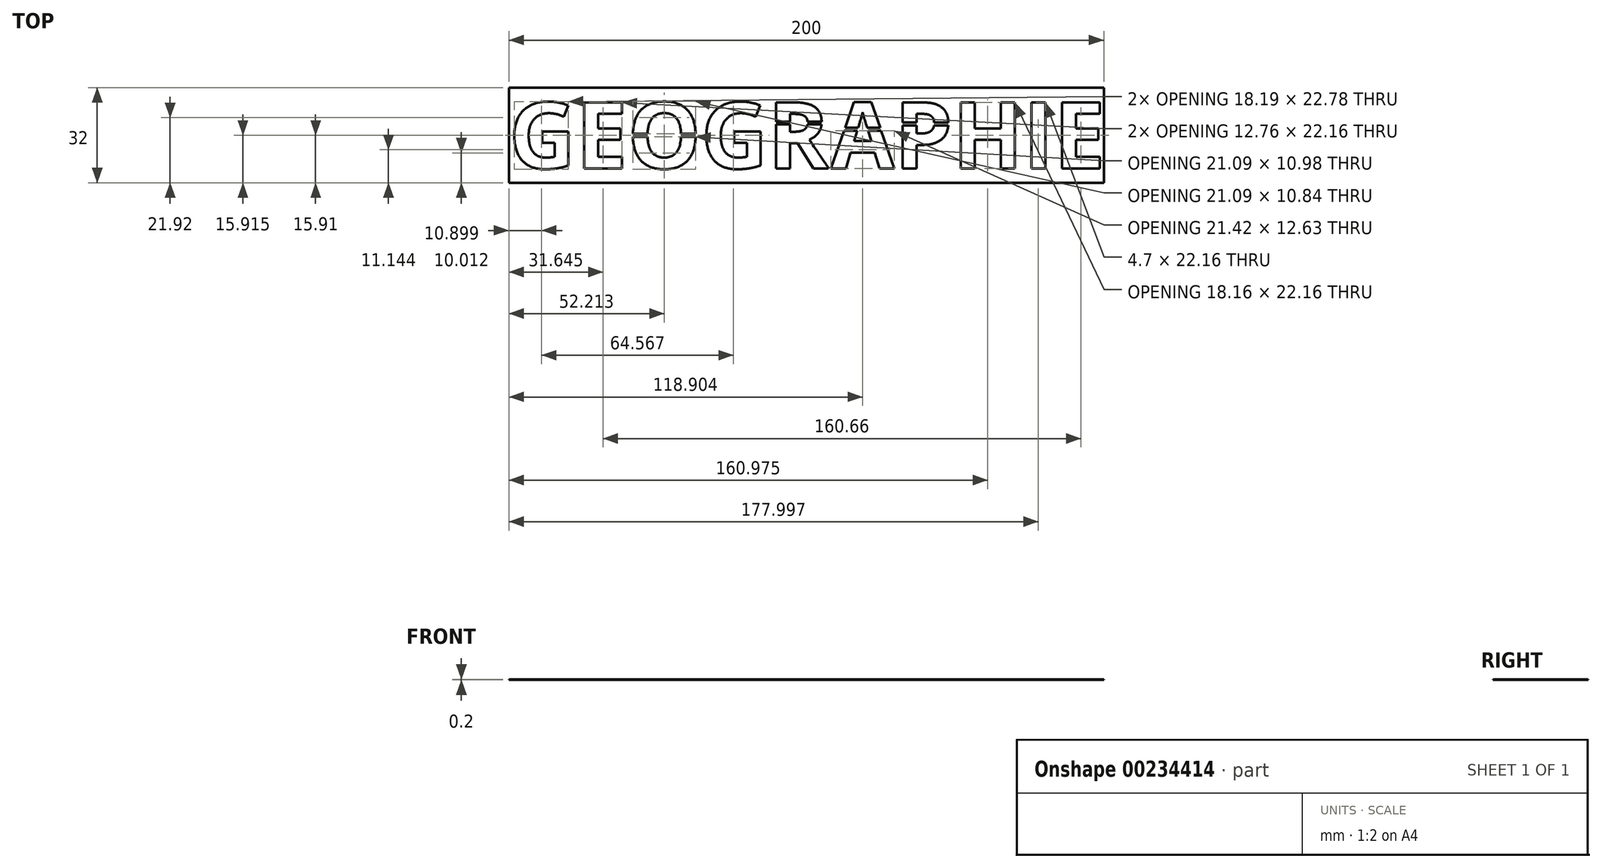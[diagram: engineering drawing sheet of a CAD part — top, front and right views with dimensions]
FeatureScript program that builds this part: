
annotation { "Feature Type Name" : "Feature", "Feature Type Description" : "" }
export const myFeature = defineFeature(function(context is Context, id is Id, definition is map)
    precondition{}
    {
        {
            var Q0;
            Q0=qCreatedBy(makeId("Top.planeOp"),FACE);
            var sketch = newSketch(context, id + "F0", { "sketchPlane" : qUnion([Q0])});
            skLineSegment(sketch, "E0.bottom", {"start": v(0, 0) * mm, "end": v(200, 0) * mm});
            skLineSegment(sketch, "E0.top", {"start": v(0, 32) * mm, "end": v(200, 32) * mm});
            skLineSegment(sketch, "E0.left", {"start": v(0, 0) * mm, "end": v(0, 32) * mm});
            skLineSegment(sketch, "E0.right", {"start": v(200, 0) * mm, "end": v(200, 32) * mm});
            skPoint(sketch, "E1", {"position": v(0, 16) * mm});
            skPoint(sketch, "E2", {"position": v(22.5, 32) * mm});
            skPoint(sketch, "E3", {"position": v(40, 32) * mm});
            skPoint(sketch, "E4", {"position": v(64.5, 32) * mm});
            skPoint(sketch, "E5", {"position": v(87, 32) * mm});
            skPoint(sketch, "E6", {"position": v(107.5, 32) * mm});
            skPoint(sketch, "E7", {"position": v(130, 32) * mm});
            skPoint(sketch, "E8", {"position": v(149, 32) * mm});
            skPoint(sketch, "E9", {"position": v(172, 32) * mm});
            skPoint(sketch, "E10", {"position": v(182.5, 32) * mm});
            skLineSegment(sketch, "E11", {"start": v(22.5, 32) * mm, "end": v(22.5, 0) * mm, "construction": true});
            skLineSegment(sketch, "E12", {"start": v(40, 32) * mm, "end": v(40, 0) * mm, "construction": true});
            skLineSegment(sketch, "E13", {"start": v(64.5, 32) * mm, "end": v(64.5, 0) * mm, "construction": true});
            skPoint(sketch, "E14", {"position": v(22.5, 16) * mm});
            skPoint(sketch, "E15", {"position": v(40, 16) * mm});
            skPoint(sketch, "E16", {"position": v(64.5, 16) * mm});
            skLineSegment(sketch, "E17", {"start": v(40, 16.5) * mm, "end": v(64.5, 16.5) * mm});
            skLineSegment(sketch, "E18", {"start": v(40, 16) * mm, "end": v(64.5, 16) * mm, "construction": true});
            skLineSegment(sketch, "E19.MirrorCS", {"start": v(40, 15.5) * mm, "end": v(64.5, 15.5) * mm});
            skLineSegment(sketch, "E20", {"start": v(87, 32) * mm, "end": v(87, 0) * mm, "construction": true});
            skLineSegment(sketch, "E21", {"start": v(130, 32) * mm, "end": v(130, 0) * mm, "construction": true});
            skLineSegment(sketch, "E22", {"start": v(149, 32) * mm, "end": v(149, 0) * mm, "construction": true});
            skLineSegment(sketch, "E23", {"start": v(172, 32) * mm, "end": v(172, 0) * mm, "construction": true});
            skLineSegment(sketch, "E24", {"start": v(182.5, 32) * mm, "end": v(182.5, 0) * mm, "construction": true});
            skLineSegment(sketch, "E25", {"start": v(107.7, 17.96) * mm, "end": v(130, 17.96) * mm, "construction": true});
            skLineSegment(sketch, "E26", {"start": v(107.7, 18.46) * mm, "end": v(130, 18.46) * mm});
            skLineSegment(sketch, "E27.MirrorCS", {"start": v(107.7, 17.46) * mm, "end": v(130, 17.46) * mm});
            skLineSegment(sketch, "E28", {"start": v(130, 19.8) * mm, "end": v(149, 19.8) * mm, "construction": true});
            skLineSegment(sketch, "E29", {"start": v(130, 20.3) * mm, "end": v(149, 20.3) * mm});
            skLineSegment(sketch, "E30.MirrorCS", {"start": v(130, 19.3) * mm, "end": v(149, 19.3) * mm});
            skText(sketch, "E31", { "text": "GEOGRAPHIE", "fontName": "OpenSans-Bold.ttf"});
            skLineSegment(sketch, "E32", {"start": v(107.33, 32) * mm, "end": v(107.33, 0) * mm});
            skLineSegment(sketch, "E33", {"start": v(107.7, 0) * mm, "end": v(107.7, 32) * mm});
            skLineSegment(sketch, "E34", {"start": v(87, 20.08) * mm, "end": v(107.33, 20.08) * mm, "construction": true});
            skLineSegment(sketch, "E35", {"start": v(87, 20.58) * mm, "end": v(107.33, 20.58) * mm});
            skLineSegment(sketch, "E36.MirrorCS", {"start": v(87, 19.58) * mm, "end": v(107.33, 19.58) * mm});
            const initialGuessF0  = {"E31": [0, 0.00483, 1, 0, 0.02235]};
            skSetInitialGuess(sketch, initialGuessF0);
            skSolve(sketch);
        }
        {
            var Q0;
            {var subQ5=sQuery(id+"F0.wireOp",EDGE,"E31.sketch_text.stroke-40");Q0=makeQuery(id+"F0.imprint","IMPRINT",FACE,{"disambiguationData":[TD([[makeQuery(id+"F0.imprint","IMPRINT",EDGE,{"derivedFrom":subQ5}),1.0]])]});}
            var Q1;
            {var subQ5=sQuery(id+"F0.wireOp",EDGE,"E31.sketch_text.stroke-44");var subQ9=sQuery(id+"F0.wireOp",EDGE,"E17");var subQ10=makeQuery(id+"F0.imprint","INTERSECT",VERTEX,{"derivedFrom":[subQ9,subQ5]});Q1=makeQuery(id+"F0.imprint","IMPRINT",FACE,{"disambiguationData":[TD([[makeQuery(id+"F0.imprint","IMPRINT",EDGE,{"disambiguationData":[TD([[subQ10,-1.0]])],"derivedFrom":subQ9}),-1.0]])]});}
            var Q2;
            {var subQ5=sQuery(id+"F0.wireOp",EDGE,"E31.sketch_text.stroke-43");Q2=makeQuery(id+"F0.imprint","IMPRINT",FACE,{"disambiguationData":[TD([[makeQuery(id+"F0.imprint","IMPRINT",EDGE,{"derivedFrom":subQ5}),1.0]])]});}
            var Q3;
            {var subQ0=sQuery(id+"F0.wireOp",EDGE,"E31.sketch_text.stroke-38");var subQ7=sQuery(id+"F0.wireOp",EDGE,"E17");var subQ8=makeQuery(id+"F0.imprint","INTERSECT",VERTEX,{"derivedFrom":[subQ7,subQ0]});Q3=makeQuery(id+"F0.imprint","IMPRINT",FACE,{"disambiguationData":[TD([[makeQuery(id+"F0.imprint","IMPRINT",EDGE,{"disambiguationData":[TD([[subQ8,1.0]])],"derivedFrom":subQ7}),-1.0]])]});}
            var Q4;
            {var subQ0=sQuery(id+"F0.wireOp",EDGE,"E31.sketch_text.stroke-35");var subQ3=sQuery(id+"F0.wireOp",EDGE,"E17");var subQ4=makeQuery(id+"F0.imprint","INTERSECT",VERTEX,{"derivedFrom":[subQ3,subQ0]});Q4=makeQuery(id+"F0.imprint","IMPRINT",FACE,{"disambiguationData":[TD([[makeQuery(id+"F0.imprint","IMPRINT",EDGE,{"disambiguationData":[TD([[subQ4,-1.0]])],"derivedFrom":subQ3}),-1.0]])]});}
            var Q5;
            Q5=makeQuery(id+"F0.imprint","IMPRINT",FACE,{"disambiguationData":[TD([[makeQuery(id+"F0.imprint","IMPRINT",EDGE,{"derivedFrom":sQuery(id+"F0.wireOp",EDGE,"E31.sketch_text.stroke-64")}),1.0]])]});
            var Q6;
            Q6=makeQuery(id+"F0.imprint","IMPRINT",FACE,{"disambiguationData":[TD([[makeQuery(id+"F0.imprint","IMPRINT",EDGE,{"derivedFrom":sQuery(id+"F0.wireOp",EDGE,"E31.sketch_text.stroke-91")}),1.0]])]});
            var Q7;
            Q7=makeQuery(id+"F0.imprint","IMPRINT",FACE,{"disambiguationData":[TD([[makeQuery(id+"F0.imprint","IMPRINT",EDGE,{"derivedFrom":sQuery(id+"F0.wireOp",EDGE,"E31.sketch_text.stroke-95")}),1.0]])]});
            var Q8;
            {var subQ16=sQuery(id+"F0.wireOp",EDGE,"E0.left");Q8=makeQuery(id+"F0.imprint","IMPRINT",FACE,{"disambiguationData":[TD([[makeQuery(id+"F0.imprint","IMPRINT",EDGE,{"derivedFrom":subQ16}),-1.0]])]});}
            var Q9;
            {var subQ0=sQuery(id+"F0.wireOp",EDGE,"E0.right");Q9=makeQuery(id+"F0.imprint","IMPRINT",FACE,{"disambiguationData":[TD([[makeQuery(id+"F0.imprint","IMPRINT",EDGE,{"derivedFrom":subQ0}),1.0]])]});}
            var Q10;
            {var subQ0=sQuery(id+"F0.wireOp",EDGE,"E32");var subQ1=sQuery(id+"F0.wireOp",EDGE,"E0.bottom");var subQ2=makeQuery(id+"F0.imprint","INTERSECT",VERTEX,{"derivedFrom":[subQ1,subQ0]});Q10=makeQuery(id+"F0.imprint","IMPRINT",FACE,{"disambiguationData":[TD([[makeQuery(id+"F0.imprint","IMPRINT",EDGE,{"disambiguationData":[TD([[subQ2,-1.0]])],"derivedFrom":subQ1}),1.0]])]});}
            var Q11;
            {var subQ0=sQuery(id+"F0.wireOp",EDGE,"E32");var subQ1=sQuery(id+"F0.wireOp",EDGE,"E0.top");var subQ2=makeQuery(id+"F0.imprint","INTERSECT",VERTEX,{"derivedFrom":[subQ1,subQ0]});Q11=makeQuery(id+"F0.imprint","IMPRINT",FACE,{"disambiguationData":[TD([[makeQuery(id+"F0.imprint","IMPRINT",EDGE,{"disambiguationData":[TD([[subQ2,-1.0]])],"derivedFrom":subQ1}),-1.0]])]});}
            var Q12;
            {var subQ1=sQuery(id+"F0.wireOp",EDGE,"E31.sketch_text.stroke-86");var subQ3=sQuery(id+"F0.wireOp",EDGE,"E33");var subQ4=makeQuery(id+"F0.imprint","INTERSECT",VERTEX,{"derivedFrom":[subQ1,subQ3]});Q12=makeQuery(id+"F0.imprint","IMPRINT",FACE,{"disambiguationData":[TD([[makeQuery(id+"F0.imprint","IMPRINT",EDGE,{"disambiguationData":[TD([[subQ4,-1.0]])],"derivedFrom":subQ3}),1.0]])]});}
            var Q13;
            {var subQ1=sQuery(id+"F0.wireOp",EDGE,"E31.sketch_text.stroke-79");var subQ3=sQuery(id+"F0.wireOp",EDGE,"E32");var subQ4=makeQuery(id+"F0.imprint","INTERSECT",VERTEX,{"derivedFrom":[subQ1,subQ3]});Q13=makeQuery(id+"F0.imprint","IMPRINT",FACE,{"disambiguationData":[TD([[makeQuery(id+"F0.imprint","IMPRINT",EDGE,{"disambiguationData":[TD([[subQ4,-1.0]])],"derivedFrom":subQ3}),1.0]])]});}
            var Q14;
            {var subQ0=sQuery(id+"F0.wireOp",EDGE,"E33");var subQ1=sQuery(id+"F0.wireOp",EDGE,"E27.MirrorCS");var subQ2=makeQuery(id+"F0.imprint","INTERSECT",VERTEX,{"derivedFrom":[subQ1,subQ0]});Q14=makeQuery(id+"F0.imprint","IMPRINT",FACE,{"disambiguationData":[TD([[makeQuery(id+"F0.imprint","IMPRINT",EDGE,{"disambiguationData":[TD([[subQ2,-1.0]])],"derivedFrom":subQ1}),-1.0]])]});}
            var Q15;
            {var subQ0=sQuery(id+"F0.wireOp",EDGE,"E33");var subQ1=sQuery(id+"F0.wireOp",EDGE,"E26");var subQ2=makeQuery(id+"F0.imprint","INTERSECT",VERTEX,{"derivedFrom":[subQ1,subQ0]});Q15=makeQuery(id+"F0.imprint","IMPRINT",FACE,{"disambiguationData":[TD([[makeQuery(id+"F0.imprint","IMPRINT",EDGE,{"disambiguationData":[TD([[subQ2,-1.0]])],"derivedFrom":subQ1}),-1.0]])]});}
            var Q16;
            {var subQ0=sQuery(id+"F0.wireOp",EDGE,"E31.sketch_text.stroke-87");var subQ1=sQuery(id+"F0.wireOp",EDGE,"E26");var subQ2=makeQuery(id+"F0.imprint","INTERSECT",VERTEX,{"derivedFrom":[subQ1,subQ0]});Q16=makeQuery(id+"F0.imprint","IMPRINT",FACE,{"disambiguationData":[TD([[makeQuery(id+"F0.imprint","IMPRINT",EDGE,{"disambiguationData":[TD([[subQ2,-1.0]])],"derivedFrom":subQ1}),-1.0]])]});}
            var Q17;
            {var subQ0=sQuery(id+"F0.wireOp",EDGE,"E31.sketch_text.stroke-89");var subQ1=sQuery(id+"F0.wireOp",EDGE,"E26");var subQ2=makeQuery(id+"F0.imprint","INTERSECT",VERTEX,{"derivedFrom":[subQ1,subQ0]});Q17=makeQuery(id+"F0.imprint","IMPRINT",FACE,{"disambiguationData":[TD([[makeQuery(id+"F0.imprint","IMPRINT",EDGE,{"disambiguationData":[TD([[subQ2,1.0]])],"derivedFrom":subQ1}),-1.0]])]});}
            var Q18;
            {var subQ0=sQuery(id+"F0.wireOp",EDGE,"E31.sketch_text.stroke-107");var subQ1=sQuery(id+"F0.wireOp",EDGE,"E29");var subQ2=makeQuery(id+"F0.imprint","INTERSECT",VERTEX,{"derivedFrom":[subQ1,subQ0]});Q18=makeQuery(id+"F0.imprint","IMPRINT",FACE,{"disambiguationData":[TD([[makeQuery(id+"F0.imprint","IMPRINT",EDGE,{"disambiguationData":[TD([[subQ2,-1.0]])],"derivedFrom":subQ1}),-1.0]])]});}
            var Q19;
            {var subQ3=sQuery(id+"F0.wireOp",EDGE,"E29");var subQ5=sQuery(id+"F0.wireOp",EDGE,"E31.sketch_text.stroke-101");var subQ9=makeQuery(id+"F0.imprint","INTERSECT",VERTEX,{"derivedFrom":[subQ3,subQ5]});Q19=makeQuery(id+"F0.imprint","IMPRINT",FACE,{"disambiguationData":[TD([[makeQuery(id+"F0.imprint","IMPRINT",EDGE,{"disambiguationData":[TD([[subQ9,-1.0]])],"derivedFrom":subQ3}),-1.0]])]});}
            var Q20;
            {var subQ1=sQuery(id+"F0.wireOp",EDGE,"E31.sketch_text.stroke-99");Q20=makeQuery(id+"F0.imprint","IMPRINT",FACE,{"disambiguationData":[TD([[makeQuery(id+"F0.imprint","IMPRINT",EDGE,{"derivedFrom":subQ1}),1.0]])]});}
            var Q21;
            {var subQ3=sQuery(id+"F0.wireOp",EDGE,"E29");var subQ9=sQuery(id+"F0.wireOp",EDGE,"E31.sketch_text.stroke-110");var subQ10=makeQuery(id+"F0.imprint","INTERSECT",VERTEX,{"derivedFrom":[subQ3,subQ9]});Q21=makeQuery(id+"F0.imprint","IMPRINT",FACE,{"disambiguationData":[TD([[makeQuery(id+"F0.imprint","IMPRINT",EDGE,{"disambiguationData":[TD([[subQ10,1.0]])],"derivedFrom":subQ3}),-1.0]])]});}
            var Q22;
            {var subQ1=sQuery(id+"F0.wireOp",EDGE,"E31.sketch_text.stroke-67");Q22=makeQuery(id+"F0.imprint","IMPRINT",FACE,{"disambiguationData":[TD([[makeQuery(id+"F0.imprint","IMPRINT",EDGE,{"derivedFrom":subQ1}),1.0]])]});}
            var Q23;
            {var subQ0=sQuery(id+"F0.wireOp",EDGE,"E35");var subQ1=sQuery(id+"F0.wireOp",EDGE,"E31.sketch_text.stroke-70");var subQ2=makeQuery(id+"F0.imprint","INTERSECT",VERTEX,{"derivedFrom":[subQ1,subQ0]});Q23=makeQuery(id+"F0.imprint","IMPRINT",FACE,{"disambiguationData":[TD([[makeQuery(id+"F0.imprint","IMPRINT",EDGE,{"disambiguationData":[TD([[subQ2,-1.0]])],"derivedFrom":subQ1}),-1.0]])]});}
            var Q24;
            {var subQ5=sQuery(id+"F0.wireOp",EDGE,"E31.sketch_text.stroke-67");var subQ6=sQuery(id+"F0.wireOp",EDGE,"E31.sketch_text.stroke-66");var subQ7=makeQuery(id+"F0.imprint","INTERSECT",VERTEX,{"derivedFrom":[subQ6,subQ5]});Q24=makeQuery(id+"F0.imprint","IMPRINT",FACE,{"disambiguationData":[TD([[makeQuery(id+"F0.imprint","IMPRINT",EDGE,{"disambiguationData":[TD([[subQ7,1.0]])],"derivedFrom":subQ6}),-1.0]])]});}
            var Q25;
            {var subQ3=sQuery(id+"F0.wireOp",EDGE,"E31.sketch_text.stroke-76");var subQ7=sQuery(id+"F0.wireOp",EDGE,"E31.sketch_text.stroke-77");var subQ8=makeQuery(id+"F0.imprint","INTERSECT",VERTEX,{"derivedFrom":[subQ3,subQ7]});Q25=makeQuery(id+"F0.imprint","IMPRINT",FACE,{"disambiguationData":[TD([[makeQuery(id+"F0.imprint","IMPRINT",EDGE,{"disambiguationData":[TD([[subQ8,1.0]])],"derivedFrom":subQ3}),1.0]])]});}
            var Q26;
            {var subQ5=sQuery(id+"F0.wireOp",EDGE,"E31.sketch_text.stroke-78");Q26=makeQuery(id+"F0.imprint","IMPRINT",FACE,{"disambiguationData":[TD([[makeQuery(id+"F0.imprint","IMPRINT",EDGE,{"derivedFrom":subQ5}),1.0]])]});}
            extrude(context, id + "F1", {"entities" : qUnion([Q0, Q1, Q2, Q3, Q4, Q5, Q6, Q7, Q8, Q9, Q10, Q11, Q12, Q13, Q14, Q15, Q16, Q17, Q18, Q19, Q20, Q21, Q22, Q23, Q24, Q25, Q26]), "depth" : 0.2 * mm});
        }
    });
